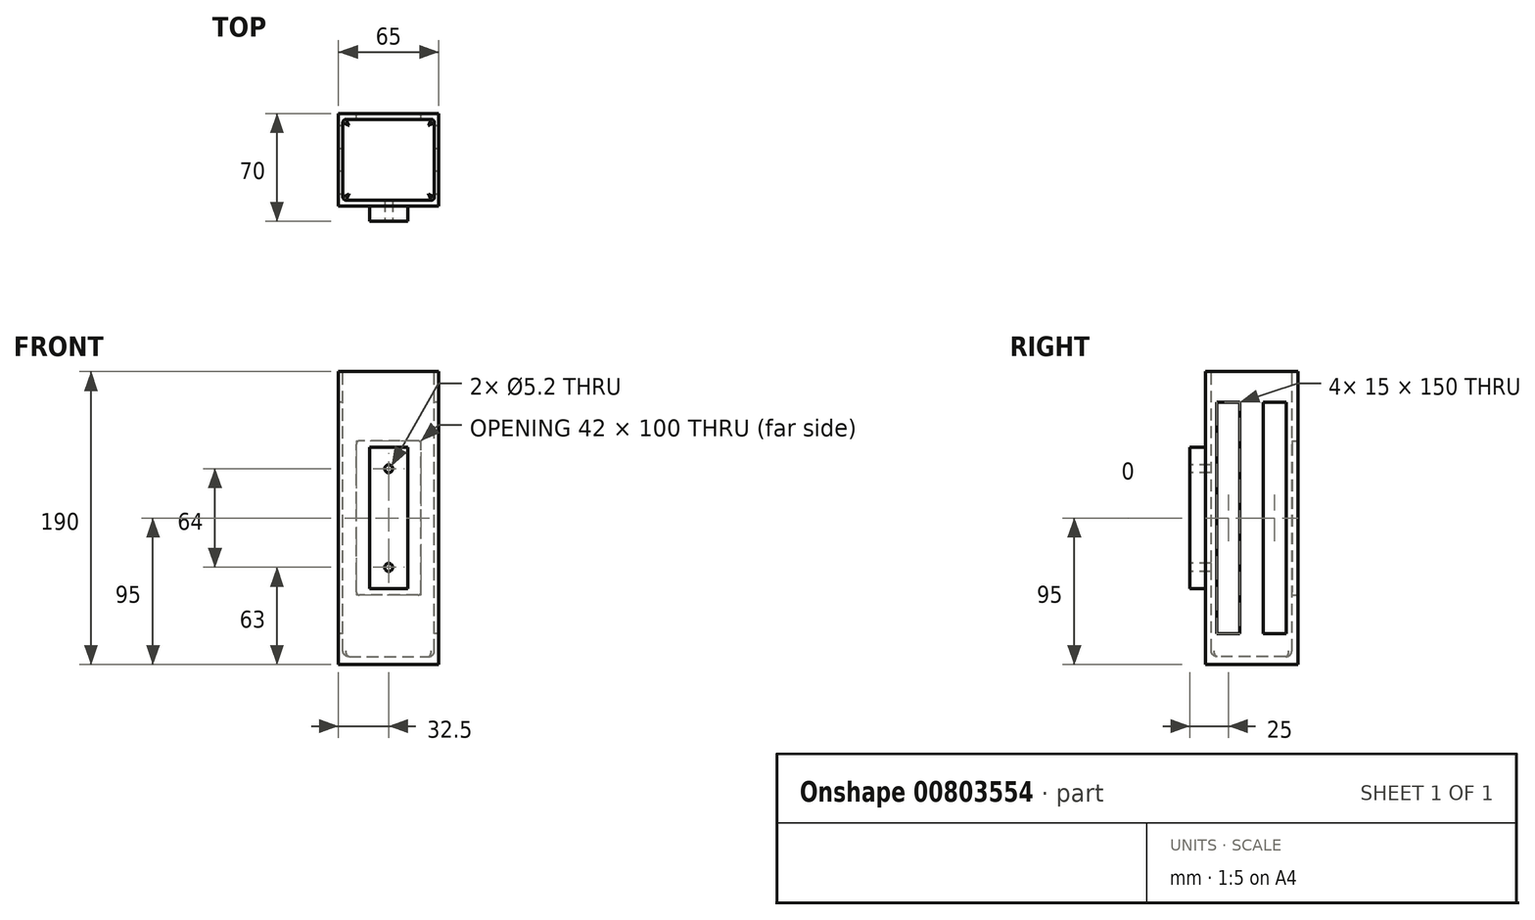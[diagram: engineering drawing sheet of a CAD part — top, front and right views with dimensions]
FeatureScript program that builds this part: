
annotation { "Feature Type Name" : "Feature", "Feature Type Description" : "" }
export const myFeature = defineFeature(function(context is Context, id is Id, definition is map)
    precondition{}
    {
        {
            var Q0;
            Q0=qCreatedBy(makeId("Top.planeOp"),FACE);
            var sketch = newSketch(context, id + "F0", { "sketchPlane" : qUnion([Q0])});
            skLineSegment(sketch, "E0.bottom", {"start": v(-32.5, 30) * mm, "end": v(32.5, 30) * mm});
            skLineSegment(sketch, "E0.top", {"start": v(-32.5, -30) * mm, "end": v(32.5, -30) * mm});
            skLineSegment(sketch, "E0.left", {"start": v(-32.5, 30) * mm, "end": v(-32.5, -30) * mm});
            skLineSegment(sketch, "E0.right", {"start": v(32.5, 30) * mm, "end": v(32.5, -30) * mm});
            skPoint(sketch, "E0.middle", {"position": v(0, 0) * mm});
            skSolve(sketch);
        }
        {
            var Q0;
            Q0 = qSketchRegion(id + "F0", true);
            extrude(context, id + "F1", {"entities" : qUnion([Q0]), "depth" : 190 * mm, "offsetDistance" : 25 * mm});
        }
        {
            var Q0;
            Q0=makeQuery(id+"F1.opExtrude","CAP_FACE",FACE,{"disambiguationData":[OSD([sQuery(id+"F0.wireOp",EDGE,"E0.bottom"),sQuery(id+"F0.wireOp",EDGE,"E0.top"),sQuery(id+"F0.wireOp",EDGE,"E0.left"),sQuery(id+"F0.wireOp",EDGE,"E0.right")])],"isStart":false});
            var sketch = newSketch(context, id + "F2", { "sketchPlane" : qUnion([Q0])});
            skLineSegment(sketch, "E1.bottom", {"start": v(-29.7, 26.2) * mm, "end": v(29.7, 26.2) * mm});
            skLineSegment(sketch, "E1.top", {"start": v(-29.7, -26.2) * mm, "end": v(29.7, -26.2) * mm});
            skLineSegment(sketch, "E1.left", {"start": v(-29.7, 26.2) * mm, "end": v(-29.7, -26.2) * mm});
            skLineSegment(sketch, "E1.right", {"start": v(29.7, 26.2) * mm, "end": v(29.7, -26.2) * mm});
            skPoint(sketch, "E1.middle", {"position": v(0, 0) * mm});
            skSolve(sketch);
        }
        {
            var Q0;
            Q0 = qSketchRegion(id + "F2", true);
            extrude(context, id + "F3", {"entities" : qUnion([Q0]), "operationType" : NewBodyOperationType.REMOVE, "oppositeDirection" : true, "depth" : 185 * mm, "offsetDistance" : 25 * mm});
        }
        {
            var Q0;
            Q0=makeQuery(id+"F1.opExtrude","SWEPT_FACE",FACE,{"disambiguationData":[OSD([sQuery(id+"F0.wireOp",EDGE,"E0.bottom")])]});
            var sketch = newSketch(context, id + "F4", { "sketchPlane" : qUnion([Q0])});
            skLineSegment(sketch, "E2.bottom", {"start": v(-21, 45) * mm, "end": v(21, 45) * mm});
            skLineSegment(sketch, "E2.top", {"start": v(-21, 145) * mm, "end": v(21, 145) * mm});
            skLineSegment(sketch, "E2.left", {"start": v(-21, 45) * mm, "end": v(-21, 145) * mm});
            skLineSegment(sketch, "E2.right", {"start": v(21, 45) * mm, "end": v(21, 145) * mm});
            skPoint(sketch, "E2.middle", {"position": v(0, 95) * mm});
            skPoint(sketch, "E2.middle.positionSnap0", {"position": v(-32.5, 95) * mm});
            skPoint(sketch, "E2.middle.positionSnap1", {"position": v(0, 0) * mm});
            skPoint(sketch, "E2.centerSnap0", {"position": v(-32.5, 95) * mm});
            skPoint(sketch, "E2.centerSnap1", {"position": v(0, 0) * mm});
            skSolve(sketch);
        }
        {
            var Q0;
            Q0 = qSketchRegion(id + "F4", true);
            extrude(context, id + "F5", {"entities" : qUnion([Q0]), "operationType" : NewBodyOperationType.REMOVE, "oppositeDirection" : true, "depth" : 20 * mm, "offsetDistance" : 25 * mm});
        }
        {
            var Q0;
            Q0=makeQuery(id+"F5.boolean.opBoolean","COPY",EDGE,{"derivedFrom":makeQuery(id+"F5.opExtrude","SWEPT_EDGE",EDGE,{"disambiguationData":[OSD([sQuery(id+"F4.wireOp",EDGE,"E2.bottom"),sQuery(id+"F4.wireOp",EDGE,"E2.left")])]})});
            var Q1;
            Q1=makeQuery(id+"F5.boolean.opBoolean","COPY",EDGE,{"derivedFrom":makeQuery(id+"F5.opExtrude","SWEPT_EDGE",EDGE,{"disambiguationData":[OSD([sQuery(id+"F4.wireOp",EDGE,"E2.bottom"),sQuery(id+"F4.wireOp",EDGE,"E2.right")])]})});
            var Q2;
            Q2=makeQuery(id+"F5.boolean.opBoolean","COPY",EDGE,{"derivedFrom":makeQuery(id+"F5.opExtrude","SWEPT_EDGE",EDGE,{"disambiguationData":[OSD([sQuery(id+"F4.wireOp",EDGE,"E2.top"),sQuery(id+"F4.wireOp",EDGE,"E2.right")])]})});
            var Q3;
            Q3=makeQuery(id+"F5.boolean.opBoolean","COPY",EDGE,{"derivedFrom":makeQuery(id+"F5.opExtrude","SWEPT_EDGE",EDGE,{"disambiguationData":[OSD([sQuery(id+"F4.wireOp",EDGE,"E2.top"),sQuery(id+"F4.wireOp",EDGE,"E2.left")])]})});
            fillet(context, id + "F6", {"entities" : qUnion([Q0, Q1, Q2, Q3]), "radius" : 2 * mm, "tangentPropagation" : true, "allowEdgeOverflow" : false});
        }
        {
            var Q0;
            Q0=makeQuery(id+"F3.boolean.opBoolean","COPY",EDGE,{"derivedFrom":makeQuery(id+"F3.opExtrude","CAP_EDGE",EDGE,{"disambiguationData":[OSD([sQuery(id+"F2.wireOp",EDGE,"E1.right")])],"isStart":false})});
            var Q1;
            Q1=makeQuery(id+"F3.boolean.opBoolean","COPY",EDGE,{"derivedFrom":makeQuery(id+"F3.opExtrude","CAP_EDGE",EDGE,{"disambiguationData":[OSD([sQuery(id+"F2.wireOp",EDGE,"E1.top")])],"isStart":false})});
            var Q2;
            Q2=makeQuery(id+"F3.boolean.opBoolean","COPY",EDGE,{"derivedFrom":makeQuery(id+"F3.opExtrude","CAP_EDGE",EDGE,{"disambiguationData":[OSD([sQuery(id+"F2.wireOp",EDGE,"E1.left")])],"isStart":false})});
            var Q3;
            Q3=makeQuery(id+"F3.boolean.opBoolean","COPY",EDGE,{"derivedFrom":makeQuery(id+"F3.opExtrude","CAP_EDGE",EDGE,{"disambiguationData":[OSD([sQuery(id+"F2.wireOp",EDGE,"E1.bottom")])],"isStart":false})});
            fillet(context, id + "F7", {"entities" : qUnion([Q0, Q1, Q2, Q3]), "radius" : 4 * mm, "tangentPropagation" : true, "allowEdgeOverflow" : false});
        }
        {
            var Q0;
            Q0=makeQuery(id+"F3.boolean.opBoolean","COPY",EDGE,{"derivedFrom":makeQuery(id+"F3.opExtrude","SWEPT_EDGE",EDGE,{"disambiguationData":[OSD([sQuery(id+"F2.wireOp",EDGE,"E1.top"),sQuery(id+"F2.wireOp",EDGE,"E1.right")])]})});
            var Q1;
            Q1=makeQuery(id+"F3.boolean.opBoolean","COPY",EDGE,{"derivedFrom":makeQuery(id+"F3.opExtrude","SWEPT_EDGE",EDGE,{"disambiguationData":[OSD([sQuery(id+"F2.wireOp",EDGE,"E1.bottom"),sQuery(id+"F2.wireOp",EDGE,"E1.right")])]})});
            var Q2;
            Q2=makeQuery(id+"F3.boolean.opBoolean","COPY",EDGE,{"derivedFrom":makeQuery(id+"F3.opExtrude","SWEPT_EDGE",EDGE,{"disambiguationData":[OSD([sQuery(id+"F2.wireOp",EDGE,"E1.top"),sQuery(id+"F2.wireOp",EDGE,"E1.left")])]})});
            var Q3;
            Q3=makeQuery(id+"F3.boolean.opBoolean","COPY",EDGE,{"derivedFrom":makeQuery(id+"F3.opExtrude","SWEPT_EDGE",EDGE,{"disambiguationData":[OSD([sQuery(id+"F2.wireOp",EDGE,"E1.bottom"),sQuery(id+"F2.wireOp",EDGE,"E1.left")])]})});
            fillet(context, id + "F8", {"entities" : qUnion([Q0, Q1, Q2, Q3]), "radius" : 2 * mm, "tangentPropagation" : true, "allowEdgeOverflow" : false});
        }
        {
            var Q0;
            Q0=makeQuery(id+"F1.opExtrude","SWEPT_FACE",FACE,{"disambiguationData":[OSD([sQuery(id+"F0.wireOp",EDGE,"E0.left")])]});
            var sketch = newSketch(context, id + "F9", { "sketchPlane" : qUnion([Q0])});
            skLineSegment(sketch, "E3", {"start": v(0, 0) * mm, "end": v(-30, 0) * mm});
            skLineSegment(sketch, "E4", {"start": v(0, 0) * mm, "end": v(30, 0) * mm});
            skLineSegment(sketch, "E5.bottom", {"start": v(22.5, 20) * mm, "end": v(7.5, 20) * mm});
            skLineSegment(sketch, "E5.top", {"start": v(22.5, 170) * mm, "end": v(7.5, 170) * mm});
            skLineSegment(sketch, "E5.left", {"start": v(22.5, 20) * mm, "end": v(22.5, 170) * mm});
            skLineSegment(sketch, "E5.right", {"start": v(7.5, 20) * mm, "end": v(7.5, 170) * mm});
            skPoint(sketch, "E5.middle", {"position": v(15, 95) * mm});
            skPoint(sketch, "E5.middle.positionSnap0", {"position": v(30, 95) * mm});
            skPoint(sketch, "E5.middle.positionSnap1", {"position": v(15, 0) * mm});
            skPoint(sketch, "E5.centerSnap0", {"position": v(30, 95) * mm});
            skPoint(sketch, "E5.centerSnap1", {"position": v(15, 0) * mm});
            skSolve(sketch);
        }
        {
            var Q0;
            Q0=makeQuery(id+"F9.imprint","IMPRINT",FACE,{"disambiguationData":[TD([[makeQuery(id+"F9.imprint","IMPRINT",EDGE,{"derivedFrom":sQuery(id+"F9.wireOp",EDGE,"E5.bottom")}),-1.0]])]});
            extrude(context, id + "F10", {"entities" : qUnion([Q0]), "operationType" : NewBodyOperationType.REMOVE, "oppositeDirection" : true, "depth" : 400 * mm, "offsetDistance" : 25 * mm});
        }
        {
            var Q0;
            Q0=makeQuery(id+"F1.opExtrude","SWEPT_FACE",FACE,{"disambiguationData":[OSD([sQuery(id+"F0.wireOp",EDGE,"E0.right")])]});
            var sketch = newSketch(context, id + "F11", { "sketchPlane" : qUnion([Q0])});
            skLineSegment(sketch, "E6.bottom", {"start": v(7.5, 170) * mm, "end": v(22.5, 170) * mm});
            skLineSegment(sketch, "E6.top", {"start": v(7.5, 20) * mm, "end": v(22.5, 20) * mm});
            skLineSegment(sketch, "E6.left", {"start": v(7.5, 170) * mm, "end": v(7.5, 20) * mm});
            skLineSegment(sketch, "E6.right", {"start": v(22.5, 170) * mm, "end": v(22.5, 20) * mm});
            skPoint(sketch, "E6.middle", {"position": v(15, 95) * mm});
            skPoint(sketch, "E6.middle.positionSnap0", {"position": v(30, 95) * mm});
            skPoint(sketch, "E6.centerSnap0", {"position": v(30, 95) * mm});
            skSolve(sketch);
        }
        {
            var Q0;
            Q0 = qSketchRegion(id + "F11", true);
            extrude(context, id + "F12", {"entities" : qUnion([Q0]), "operationType" : NewBodyOperationType.REMOVE, "oppositeDirection" : true, "depth" : 400 * mm, "offsetDistance" : 25 * mm});
        }
        {
            var Q0;
            Q0=makeQuery(id+"F1.opExtrude","SWEPT_FACE",FACE,{"disambiguationData":[OSD([sQuery(id+"F0.wireOp",EDGE,"E0.top")])]});
            var sketch = newSketch(context, id + "F13", { "sketchPlane" : qUnion([Q0])});
            skLineSegment(sketch, "E7", {"start": v(0, 95) * mm, "end": v(0, 127) * mm});
            skPoint(sketch, "E7.startSnap0", {"position": v(-32.5, 95) * mm});
            skPoint(sketch, "E7.startSnap1", {"position": v(0, 190) * mm});
            skCircle(sketch, "E8", {"center": v(0, 127) * mm, "radius": 2.6 * mm});
            skSolve(sketch);
        }
        {
            var Q0;
            Q0 = qSketchRegion(id + "F13", true);
            extrude(context, id + "F14", {"entities" : qUnion([Q0]), "operationType" : NewBodyOperationType.REMOVE, "oppositeDirection" : true, "depth" : 25 * mm, "offsetDistance" : 25 * mm});
        }
        {
            var Q0;
            Q0=makeQuery(id+"F1.opExtrude","SWEPT_FACE",FACE,{"disambiguationData":[OSD([sQuery(id+"F0.wireOp",EDGE,"E0.top")])]});
            var sketch = newSketch(context, id + "F15", { "sketchPlane" : qUnion([Q0])});
            skLineSegment(sketch, "E9", {"start": v(0, 95) * mm, "end": v(0, 63) * mm});
            skPoint(sketch, "E9.startSnap0", {"position": v(-32.5, 95) * mm});
            skCircle(sketch, "E10", {"center": v(0, 63) * mm, "radius": 2.6 * mm});
            skSolve(sketch);
        }
        {
            var Q0;
            Q0 = qSketchRegion(id + "F15", true);
            extrude(context, id + "F16", {"entities" : qUnion([Q0]), "operationType" : NewBodyOperationType.REMOVE, "oppositeDirection" : true, "depth" : 25 * mm, "offsetDistance" : 25 * mm});
        }
        {
            var Q0;
            Q0=makeQuery(id+"F1.opExtrude","SWEPT_FACE",FACE,{"disambiguationData":[OSD([sQuery(id+"F0.wireOp",EDGE,"E0.top")])]});
            var sketch = newSketch(context, id + "F17", { "sketchPlane" : qUnion([Q0])});
            skLineSegment(sketch, "E11.bottom", {"start": v(-12.47, 140.93) * mm, "end": v(12.47, 140.93) * mm});
            skLineSegment(sketch, "E11.top", {"start": v(-12.47, 49.07) * mm, "end": v(12.47, 49.07) * mm});
            skLineSegment(sketch, "E11.left", {"start": v(-12.47, 140.93) * mm, "end": v(-12.47, 49.07) * mm});
            skLineSegment(sketch, "E11.right", {"start": v(12.47, 140.93) * mm, "end": v(12.47, 49.07) * mm});
            skPoint(sketch, "E11.middle", {"position": v(0, 95) * mm});
            skPoint(sketch, "E11.middle.positionSnap0", {"position": v(-32.5, 95) * mm});
            skPoint(sketch, "E11.centerSnap0", {"position": v(-32.5, 95) * mm});
            skSolve(sketch);
        }
        {
            var Q0;
            Q0 = qSketchRegion(id + "F17", true);
            extrude(context, id + "F18", {"entities" : qUnion([Q0]), "operationType" : NewBodyOperationType.ADD, "depth" : 10 * mm, "offsetDistance" : 25 * mm});
        }
        {
            var Q0;
            Q0=makeQuery(id+"F18.boolean.opBoolean","SPLIT",FACE,{"disambiguationData":[TD([makeQuery(id+"F14.boolean.opBoolean","COPY",FACE,{"derivedFrom":makeQuery(id+"F14.opExtrude","SWEPT_FACE",FACE,{"disambiguationData":[OSD([sQuery(id+"F13.wireOp",EDGE,"E8")])]})})])],"derivedFrom":makeQuery(id+"F18.opExtrude","CAP_FACE",FACE,{"disambiguationData":[OSD([sQuery(id+"F17.wireOp",EDGE,"E11.bottom"),sQuery(id+"F17.wireOp",EDGE,"E11.top"),sQuery(id+"F17.wireOp",EDGE,"E11.left"),sQuery(id+"F17.wireOp",EDGE,"E11.right")])],"isStart":true})});
            extrude(context, id + "F19", {"entities" : qUnion([Q0]), "operationType" : NewBodyOperationType.REMOVE, "oppositeDirection" : true, "depth" : 400 * mm, "offsetDistance" : 25 * mm});
        }
        {
            var Q0;
            Q0=makeQuery(id+"F18.boolean.opBoolean","SPLIT",FACE,{"disambiguationData":[TD([makeQuery(id+"F16.boolean.opBoolean","COPY",FACE,{"derivedFrom":makeQuery(id+"F16.opExtrude","SWEPT_FACE",FACE,{"disambiguationData":[OSD([sQuery(id+"F15.wireOp",EDGE,"E10")])]})})])],"derivedFrom":makeQuery(id+"F18.opExtrude","CAP_FACE",FACE,{"disambiguationData":[OSD([sQuery(id+"F17.wireOp",EDGE,"E11.bottom"),sQuery(id+"F17.wireOp",EDGE,"E11.top"),sQuery(id+"F17.wireOp",EDGE,"E11.left"),sQuery(id+"F17.wireOp",EDGE,"E11.right")])],"isStart":true})});
            extrude(context, id + "F20", {"entities" : qUnion([Q0]), "operationType" : NewBodyOperationType.REMOVE, "oppositeDirection" : true, "depth" : 25 * mm, "offsetDistance" : 25 * mm});
        }
    });
